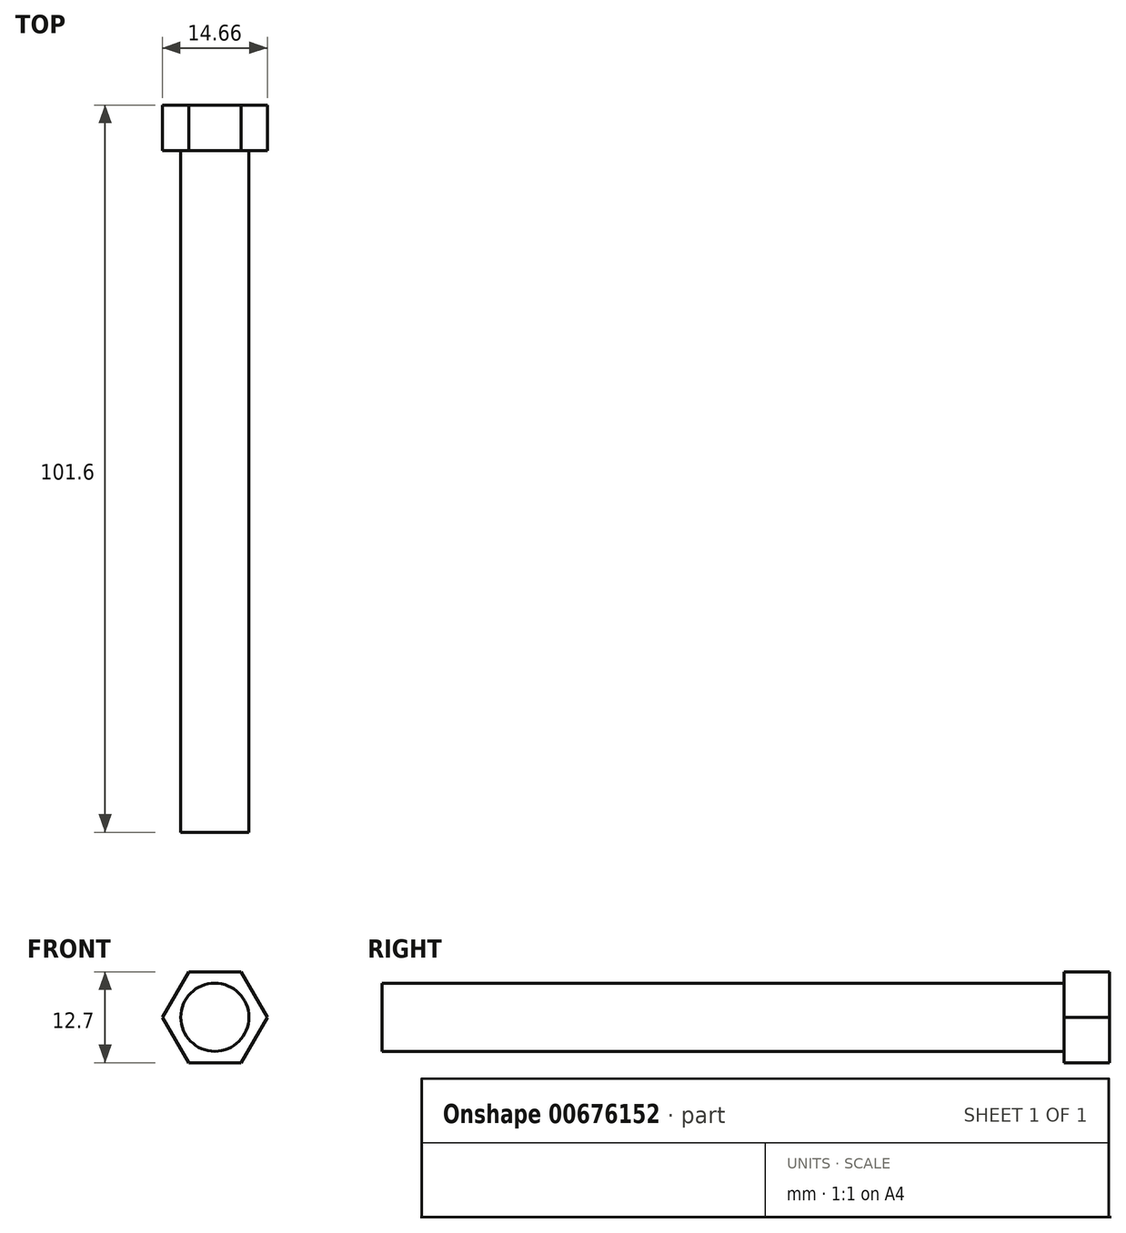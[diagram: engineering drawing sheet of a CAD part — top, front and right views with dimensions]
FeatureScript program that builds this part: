
annotation { "Feature Type Name" : "Feature", "Feature Type Description" : "" }
export const myFeature = defineFeature(function(context is Context, id is Id, definition is map)
    precondition{}
    {
        {
            var Q0;
            Q0=qCreatedBy(makeId("Front.planeOp"),FACE);
            var sketch = newSketch(context, id + "F0", { "sketchPlane" : qUnion([Q0])});
            skCircle(sketch, "E0", {"center": v(0, 0) * mm, "radius": 4.76 * mm});
            skSolve(sketch);
        }
        {
            var Q0;
            Q0=makeQuery(id+"F0.imprint","IMPRINT",FACE,{"disambiguationData":[TD([[makeQuery(id+"F0.imprint","IMPRINT",EDGE,{"derivedFrom":sQuery(id+"F0.wireOp",EDGE,"E0")}),1.0]])]});
            extrude(context, id + "F1", {"entities" : qUnion([Q0]), "depth" : 101.6 * mm, "offsetDistance" : 25.4 * mm});
        }
        {
            var Q0;
            Q0=qCreatedBy(makeId("Front.planeOp"),FACE);
            var sketch = newSketch(context, id + "F2", { "sketchPlane" : qUnion([Q0])});
            skCircle(sketch, "E1.cCircle", {"center": v(0, 0) * mm, "radius": 6.35 * mm, "construction": true});
            skLineSegment(sketch, "E1.0", {"start": v(3.67, -6.35) * mm, "end": v(-3.67, -6.35) * mm});
            skLineSegment(sketch, "E1.1", {"start": v(-3.67, -6.35) * mm, "end": v(-7.33, 0) * mm});
            skLineSegment(sketch, "E1.2", {"start": v(-7.33, 0) * mm, "end": v(-3.67, 6.35) * mm});
            skLineSegment(sketch, "E1.3", {"start": v(-3.67, 6.35) * mm, "end": v(3.67, 6.35) * mm});
            skLineSegment(sketch, "E1.4", {"start": v(3.67, 6.35) * mm, "end": v(7.33, 0) * mm});
            skLineSegment(sketch, "E1.5", {"start": v(7.33, 0) * mm, "end": v(3.67, -6.35) * mm});
            skPoint(sketch, "E1.0.midPoint", {"position": v(0, -6.35) * mm});
            skSolve(sketch);
        }
        {
            var Q0;
            Q0 = qSketchRegion(id + "F2", true);
            extrude(context, id + "F3", {"entities" : qUnion([Q0]), "operationType" : NewBodyOperationType.ADD, "depth" : 6.35 * mm, "offsetDistance" : 25.4 * mm});
        }
    });
